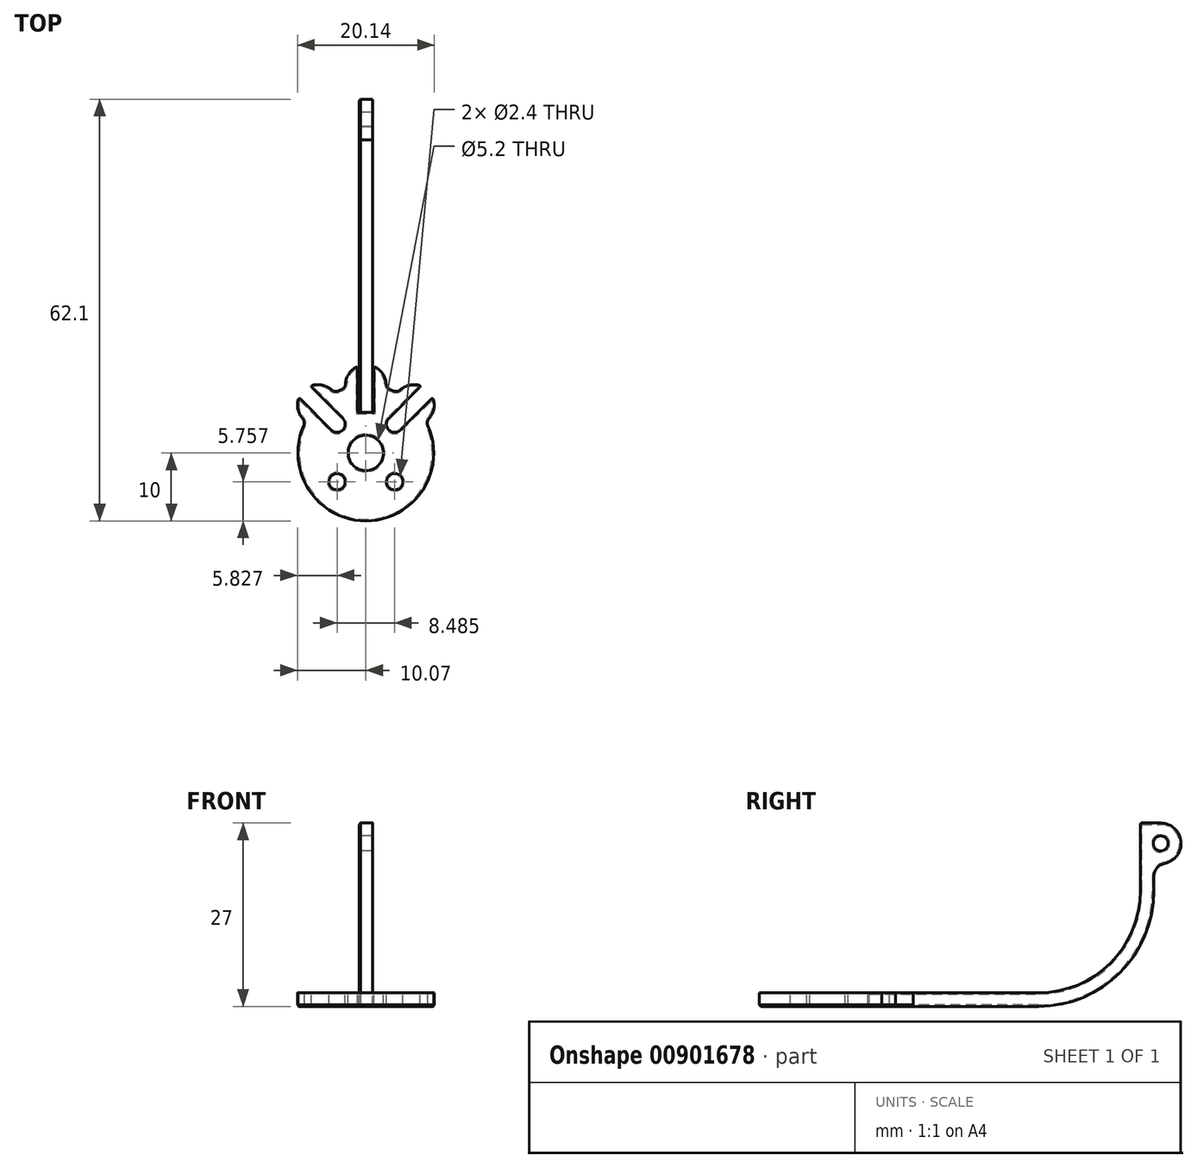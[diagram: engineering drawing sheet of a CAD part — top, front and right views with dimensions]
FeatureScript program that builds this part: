
annotation { "Feature Type Name" : "Feature", "Feature Type Description" : "" }
export const myFeature = defineFeature(function(context is Context, id is Id, definition is map)
    precondition{}
    {
        {
            var Q0;
            Q0=qCreatedBy(makeId("Top.planeOp"),FACE);
            var sketch = newSketch(context, id + "F0", { "sketchPlane" : qUnion([Q0])});
            skCircle(sketch, "E0", {"center": v(0, 0) * mm, "radius": 6 * mm, "construction": true});
            skCircle(sketch, "E1", {"center": v(0, 0) * mm, "radius": 38.1 * mm, "construction": true});
            skCircle(sketch, "E2", {"center": v(0, 0) * mm, "radius": 10 * mm, "construction": true});
            skLineSegment(sketch, "E3.bottom", {"start": v(4.24, 4.24) * mm, "end": v(-4.24, 4.24) * mm, "construction": true});
            skLineSegment(sketch, "E3.top", {"start": v(4.24, -4.24) * mm, "end": v(-4.24, -4.24) * mm, "construction": true});
            skLineSegment(sketch, "E3.left", {"start": v(4.24, 4.24) * mm, "end": v(4.24, -4.24) * mm, "construction": true});
            skLineSegment(sketch, "E3.right", {"start": v(-4.24, 4.24) * mm, "end": v(-4.24, -4.24) * mm, "construction": true});
            skCircle(sketch, "E4", {"center": v(4.24, 4.24) * mm, "radius": 1 * mm, "construction": true});
            skCircle(sketch, "E5.1.0", {"center": v(-4.24, 4.24) * mm, "radius": 1 * mm, "construction": true});
            skCircle(sketch, "E5.2.0", {"center": v(-4.24, -4.24) * mm, "radius": 1 * mm, "construction": true});
            skCircle(sketch, "E5.3.0", {"center": v(4.24, -4.24) * mm, "radius": 1 * mm, "construction": true});
            skCircle(sketch, "E6", {"center": v(0, 0) * mm, "radius": 2.5 * mm, "construction": true});
            skSolve(sketch);
        }
        {
            var Q0;
            Q0=qCreatedBy(makeId("Front.planeOp"),FACE);
            var sketch = newSketch(context, id + "F1", { "sketchPlane" : qUnion([Q0])});
            skLineSegment(sketch, "E7", {"start": v(0, 0) * mm, "end": v(0, 2) * mm});
            skSolve(sketch);
        }
        {
            var Q0;
            Q0=qCreatedBy(makeId("Top.planeOp"),FACE);
            var sketch = newSketch(context, id + "F2", { "sketchPlane" : qUnion([Q0])});
            skArc(sketch, "E8.0", {"start": v(-8.85, 4.66) * mm, "mid": v(-2.4, -9.7) * mm, "end": v(10, 0) * mm});
            skArc(sketch, "E9.1.0", {"start": v(-5.1, 3.4) * mm, "mid": v(-3.4, 3.4) * mm, "end": v(-3.4, 5.1) * mm});
            skCircle(sketch, "E9.2.0", {"center": v(-4.24, -4.24) * mm, "radius": 1.2 * mm});
            skCircle(sketch, "E9.3.0", {"center": v(4.24, -4.24) * mm, "radius": 1.2 * mm});
            skCircle(sketch, "E10.0", {"center": v(0, 0) * mm, "radius": 2.6 * mm});
            skLineSegment(sketch, "E11", {"start": v(0, 0) * mm, "end": v(-7.07, 7.07) * mm, "construction": true});
            skArc(sketch, "E12", {"start": v(-8.85, 4.66) * mm, "mid": v(-9.95, 6.24) * mm, "end": v(-9.86, 8.17) * mm});
            skLineSegment(sketch, "E13", {"start": v(-5.1, 3.4) * mm, "end": v(-9.86, 8.17) * mm});
            skLineSegment(sketch, "E14", {"start": v(-3.4, 5.1) * mm, "end": v(-8.17, 9.86) * mm});
            skArc(sketch, "E15.trimOffspring", {"start": v(-8.17, 9.86) * mm, "mid": v(-6.24, 9.95) * mm, "end": v(-4.66, 8.85) * mm});
            skPoint(sketch, "E16", {"position": v(-10, 0) * mm});
            skPoint(sketch, "E17", {"position": v(10, 0) * mm});
            skArc(sketch, "E18.1.0", {"start": v(-2.97, 9.55) * mm, "mid": v(-2.63, 11.45) * mm, "end": v(-1.2, 12.75) * mm});
            skLineSegment(sketch, "E18.1.1", {"start": v(-1.2, 6) * mm, "end": v(-1.2, 12.75) * mm});
            skLineSegment(sketch, "E18.1.2", {"start": v(1.2, 6) * mm, "end": v(1.2, 12.75) * mm});
            skArc(sketch, "E18.1.3", {"start": v(1.2, 12.75) * mm, "mid": v(2.63, 11.45) * mm, "end": v(2.97, 9.55) * mm});
            skArc(sketch, "E18.2.0", {"start": v(4.66, 8.85) * mm, "mid": v(6.24, 9.95) * mm, "end": v(8.17, 9.86) * mm});
            skLineSegment(sketch, "E18.2.1", {"start": v(3.4, 5.1) * mm, "end": v(8.17, 9.86) * mm});
            skLineSegment(sketch, "E18.2.2", {"start": v(5.1, 3.4) * mm, "end": v(9.86, 8.17) * mm});
            skArc(sketch, "E18.2.3", {"start": v(9.86, 8.17) * mm, "mid": v(9.95, 6.24) * mm, "end": v(8.85, 4.66) * mm});
            skLineSegment(sketch, "E18.anchor1", {"start": v(0, 0) * mm, "end": v(-8.85, 4.66) * mm, "construction": true});
            skLineSegment(sketch, "E18.anchor2", {"start": v(0, 0) * mm, "end": v(4.66, 8.85) * mm, "construction": true});
            skArc(sketch, "E19", {"start": v(-4.66, 8.85) * mm, "mid": v(-3.83, 9.24) * mm, "end": v(-2.97, 9.55) * mm});
            skArc(sketch, "E20", {"start": v(2.97, 9.55) * mm, "mid": v(3.83, 9.24) * mm, "end": v(4.66, 8.85) * mm});
            skArc(sketch, "E21", {"start": v(8.85, 4.66) * mm, "mid": v(9.7, 2.4) * mm, "end": v(10, 0) * mm});
            skLineSegment(sketch, "E22", {"start": v(-1.2, 6) * mm, "end": v(1.2, 6) * mm});
            skArc(sketch, "E23", {"start": v(3.4, 5.1) * mm, "mid": v(3.4, 3.4) * mm, "end": v(5.1, 3.4) * mm});
            skArc(sketch, "E24", {"start": v(5.1, 3.4) * mm, "mid": v(5.1, 5.1) * mm, "end": v(3.4, 5.1) * mm, "construction": true});
            skSolve(sketch);
        }
        {
            var Q0;
            Q0 = qSketchRegion(id + "F2", true);
            var Q1;
            Q1=sQuery(id+"F1.wireOp",EDGE,"E7");
            sweep(context, id + "F3", {"profiles" : qUnion([Q0]), "path" : qUnion([Q1])});
        }
        {
            var Q0;
            Q0=makeQuery(id+"F3.opSweep","SWEPT_EDGE",EDGE,{"disambiguationData":[OSD([sQuery(id+"F1.wireOp",EDGE,"E7"),sQuery(id+"F2.wireOp",EDGE,"E8.0"),sQuery(id+"F2.wireOp",EDGE,"E12")])]});
            var Q1;
            Q1=makeQuery(id+"F3.opSweep","SWEPT_EDGE",EDGE,{"disambiguationData":[OSD([sQuery(id+"F1.wireOp",EDGE,"E7"),sQuery(id+"F2.wireOp",EDGE,"E15.trimOffspring"),sQuery(id+"F2.wireOp",EDGE,"E19")])]});
            var Q2;
            Q2=makeQuery(id+"F3.opSweep","SWEPT_EDGE",EDGE,{"disambiguationData":[OSD([sQuery(id+"F1.wireOp",EDGE,"E7"),sQuery(id+"F2.wireOp",EDGE,"E18.1.0"),sQuery(id+"F2.wireOp",EDGE,"E19")])]});
            var Q3;
            Q3=makeQuery(id+"F3.opSweep","SWEPT_EDGE",EDGE,{"disambiguationData":[OSD([sQuery(id+"F1.wireOp",EDGE,"E7"),sQuery(id+"F2.wireOp",EDGE,"E18.1.3"),sQuery(id+"F2.wireOp",EDGE,"E20")])]});
            var Q4;
            Q4=makeQuery(id+"F3.opSweep","SWEPT_EDGE",EDGE,{"disambiguationData":[OSD([sQuery(id+"F1.wireOp",EDGE,"E7"),sQuery(id+"F2.wireOp",EDGE,"E18.2.0"),sQuery(id+"F2.wireOp",EDGE,"E20")])]});
            var Q5;
            Q5=makeQuery(id+"F3.opSweep","SWEPT_EDGE",EDGE,{"disambiguationData":[OSD([sQuery(id+"F1.wireOp",EDGE,"E7"),sQuery(id+"F2.wireOp",EDGE,"E18.2.3"),sQuery(id+"F2.wireOp",EDGE,"E21")])]});
            fillet(context, id + "F4", {"entities" : qUnion([Q0, Q1, Q2, Q3, Q4, Q5]), "radius" : 1 * mm, "allowEdgeOverflow" : false});
        }
        {
            var Q0;
            Q0=makeQuery(id+"F3.opSweep","SWEPT_EDGE",EDGE,{"disambiguationData":[OSD([sQuery(id+"F1.wireOp",EDGE,"E7"),sQuery(id+"F2.wireOp",EDGE,"E12"),sQuery(id+"F2.wireOp",EDGE,"E13")])]});
            var Q1;
            Q1=makeQuery(id+"F3.opSweep","SWEPT_EDGE",EDGE,{"disambiguationData":[OSD([sQuery(id+"F1.wireOp",EDGE,"E7"),sQuery(id+"F2.wireOp",EDGE,"E14"),sQuery(id+"F2.wireOp",EDGE,"E15.trimOffspring")])]});
            var Q2;
            Q2=makeQuery(id+"F3.opSweep","SWEPT_EDGE",EDGE,{"disambiguationData":[OSD([sQuery(id+"F1.wireOp",EDGE,"E7"),sQuery(id+"F2.wireOp",EDGE,"E18.1.0"),sQuery(id+"F2.wireOp",EDGE,"E18.1.1")])]});
            var Q3;
            Q3=makeQuery(id+"F3.opSweep","SWEPT_EDGE",EDGE,{"disambiguationData":[OSD([sQuery(id+"F1.wireOp",EDGE,"E7"),sQuery(id+"F2.wireOp",EDGE,"E18.1.2"),sQuery(id+"F2.wireOp",EDGE,"E18.1.3")])]});
            var Q4;
            Q4=makeQuery(id+"F3.opSweep","SWEPT_EDGE",EDGE,{"disambiguationData":[OSD([sQuery(id+"F1.wireOp",EDGE,"E7"),sQuery(id+"F2.wireOp",EDGE,"E18.2.0"),sQuery(id+"F2.wireOp",EDGE,"E18.2.1")])]});
            var Q5;
            Q5=makeQuery(id+"F3.opSweep","SWEPT_EDGE",EDGE,{"disambiguationData":[OSD([sQuery(id+"F1.wireOp",EDGE,"E7"),sQuery(id+"F2.wireOp",EDGE,"E18.2.2"),sQuery(id+"F2.wireOp",EDGE,"E18.2.3")])]});
            fillet(context, id + "F5", {"entities" : qUnion([Q0, Q1, Q2, Q3, Q4, Q5]), "radius" : 0.2 * mm, "tangentPropagation" : true, "allowEdgeOverflow" : false});
        }
        {
            var Q0;
            Q0=qCreatedBy(makeId("Right.planeOp"),FACE);
            var sketch = newSketch(context, id + "F6", { "sketchPlane" : qUnion([Q0])});
            skLineSegment(sketch, "E25", {"start": v(6, 0) * mm, "end": v(6, 2) * mm});
            skLineSegment(sketch, "E26.0", {"start": v(-38.1, 0) * mm, "end": v(38.1, 0) * mm, "construction": true});
            skLineSegment(sketch, "E27", {"start": v(38.1, 0) * mm, "end": v(46.1, 0) * mm, "construction": true});
            skLineSegment(sketch, "E28", {"start": v(6, 2) * mm, "end": v(31.1, 2) * mm});
            skLineSegment(sketch, "E29", {"start": v(46.1, 17) * mm, "end": v(46.1, 27) * mm});
            skLineSegment(sketch, "E30", {"start": v(46.1, 27) * mm, "end": v(49.1, 27) * mm});
            skCircle(sketch, "E31", {"center": v(49.1, 24) * mm, "radius": 1.1 * mm});
            skArc(sketch, "E32", {"start": v(49.1, 27) * mm, "mid": v(52.1, 24) * mm, "end": v(49.1, 21) * mm});
            skPoint(sketch, "E33.visualSharp", {"position": v(46.1, 2) * mm});
            skArc(sketch, "E33.filletArc", {"start": v(31.1, 2) * mm, "mid": v(41.7, 6.4) * mm, "end": v(46.1, 17) * mm});
            skLineSegment(sketch, "E34.0", {"start": v(48.1, 17) * mm, "end": v(48.1, 21) * mm});
            skArc(sketch, "E34.1", {"start": v(31.1, 0) * mm, "mid": v(43.12, 4.98) * mm, "end": v(48.1, 17) * mm});
            skLineSegment(sketch, "E34.2", {"start": v(6, 0) * mm, "end": v(31.1, 0) * mm});
            skLineSegment(sketch, "E35", {"start": v(48.1, 21) * mm, "end": v(49.1, 21) * mm});
            skSolve(sketch);
        }
        {
            var Q0;
            Q0=makeQuery(id+"F6.imprint","IMPRINT",FACE,{"disambiguationData":[TD([[makeQuery(id+"F6.imprint","IMPRINT",EDGE,{"derivedFrom":sQuery(id+"F6.wireOp",EDGE,"E25")}),-1.0]])]});
            extrude(context, id + "F7", {"entities" : qUnion([Q0]), "endBound" : BoundingType.SYMMETRIC, "depth" : 2 * mm, "offsetDistance" : 25 * mm});
        }
        {
            var Q0;
            Q0=makeQuery(id+"F7.opExtrude","SWEPT_EDGE",EDGE,{"disambiguationData":[OSD([sQuery(id+"F6.wireOp",EDGE,"E34.0"),sQuery(id+"F6.wireOp",EDGE,"E35")])]});
            fillet(context, id + "F8", {"entities" : qUnion([Q0]), "radius" : 2 * mm, "allowEdgeOverflow" : false});
        }
        {
            var Q0;
            Q0=makeQuery(id+"F7.opExtrude","SWEPT_EDGE",EDGE,{"disambiguationData":[OSD([sQuery(id+"F6.wireOp",EDGE,"E29"),sQuery(id+"F6.wireOp",EDGE,"E30")])]});
            fillet(context, id + "F9", {"entities" : qUnion([Q0]), "radius" : .2 * mm, "allowEdgeOverflow" : false});
        }
        {
            var Q0;
            Q0=makeQuery(id+"F3.opSweep","CAP_FACE",FACE,{"disambiguationData":[OSD([sQuery(id+"F1.wireOp",VERTEX,"E7.start"),sQuery(id+"F2.wireOp",EDGE,"E8.0"),sQuery(id+"F2.wireOp",EDGE,"E9.1.0"),sQuery(id+"F2.wireOp",EDGE,"E9.2.0"),sQuery(id+"F2.wireOp",EDGE,"E9.3.0"),sQuery(id+"F2.wireOp",EDGE,"E10.0"),sQuery(id+"F2.wireOp",EDGE,"E12"),sQuery(id+"F2.wireOp",EDGE,"E13"),sQuery(id+"F2.wireOp",EDGE,"E14"),sQuery(id+"F2.wireOp",EDGE,"E15.trimOffspring"),sQuery(id+"F2.wireOp",EDGE,"E18.1.0"),sQuery(id+"F2.wireOp",EDGE,"E18.1.1"),sQuery(id+"F2.wireOp",EDGE,"E18.1.2"),sQuery(id+"F2.wireOp",EDGE,"E18.1.3"),sQuery(id+"F2.wireOp",EDGE,"E18.2.0"),sQuery(id+"F2.wireOp",EDGE,"E18.2.1"),sQuery(id+"F2.wireOp",EDGE,"E18.2.2"),sQuery(id+"F2.wireOp",EDGE,"E18.2.3"),sQuery(id+"F2.wireOp",EDGE,"E19"),sQuery(id+"F2.wireOp",EDGE,"E20"),sQuery(id+"F2.wireOp",EDGE,"E21"),sQuery(id+"F2.wireOp",EDGE,"E22"),sQuery(id+"F2.wireOp",EDGE,"E23")])],"isStart":true});
            var Q1;
            Q1=makeQuery(id+"F7.opExtrude","CAP_FACE",FACE,{"disambiguationData":[OSD([sQuery(id+"F6.wireOp",EDGE,"E25"),sQuery(id+"F6.wireOp",EDGE,"E28"),sQuery(id+"F6.wireOp",EDGE,"E29"),sQuery(id+"F6.wireOp",EDGE,"E30"),sQuery(id+"F6.wireOp",EDGE,"E31"),sQuery(id+"F6.wireOp",EDGE,"E32"),sQuery(id+"F6.wireOp",EDGE,"E33.filletArc"),sQuery(id+"F6.wireOp",EDGE,"E34.0"),sQuery(id+"F6.wireOp",EDGE,"E34.1"),sQuery(id+"F6.wireOp",EDGE,"E34.2"),sQuery(id+"F6.wireOp",EDGE,"E35")])],"isStart":true});
            chamfer(context, id + "F10", {"entities" : qUnion([Q0, Q1]), "width" : 0.2 * mm});
        }
    });
